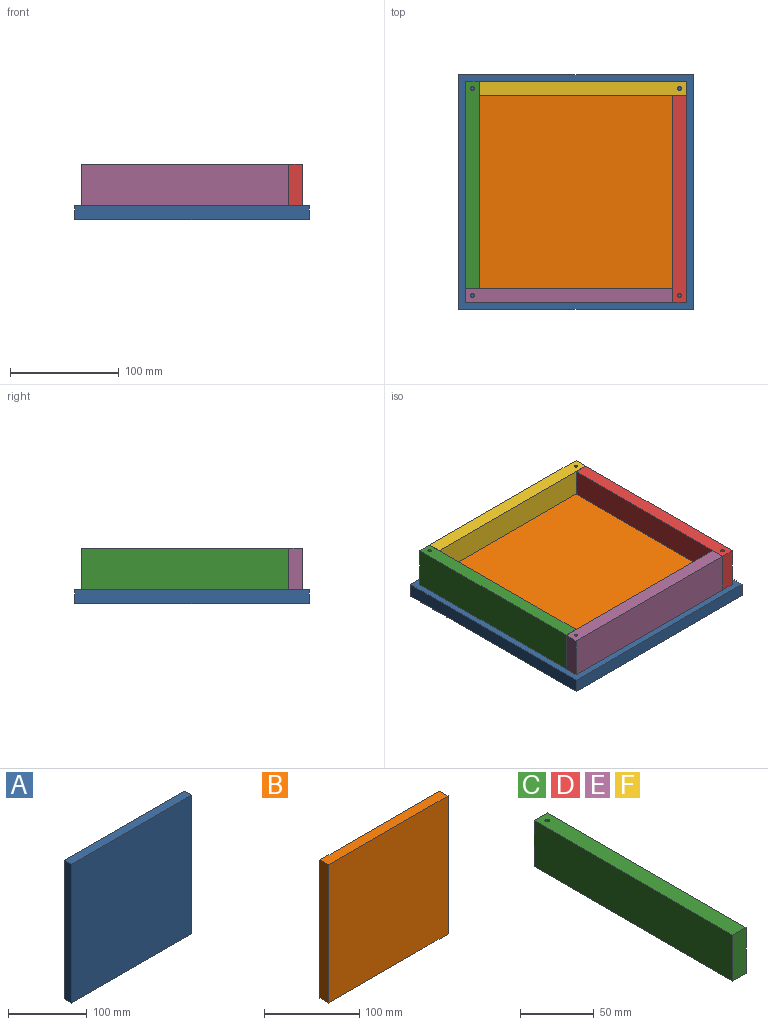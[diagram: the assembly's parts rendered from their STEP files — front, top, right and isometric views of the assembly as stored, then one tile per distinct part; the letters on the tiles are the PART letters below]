
ASSEMBLY  parts=6 mates=7
PART A: 6 faces, bbox 215.9x12.7x215.9 mm
  f0: plane 215.9x12.7mm, normal (0,0,1), area 2741.9mm2, adj f1,f3,f4,f5
  f1: plane 215.9x12.7mm, normal (-1,0,0), area 2741.9mm2, adj f0,f2,f4,f5
  f2: plane 215.9x12.7mm, normal (0,0,-1), area 2741.9mm2, adj f1,f3,f4,f5
  f3: plane 215.9x12.7mm, normal (1,0,0), area 2741.9mm2, adj f0,f2,f4,f5
  f4: plane 215.9x215.9mm, normal (0,-1,0), area 46612.8mm2, adj f0,f1,f2,f3
  f5: plane 215.9x215.9mm, normal (0,1,0), area 46612.8mm2, adj f0,f1,f2,f3
PART B: 6 faces, bbox 177.8x12.7x177.8 mm
  f0: plane 177.8x12.7mm, normal (0,0,1), area 2258.1mm2, adj f1,f3,f4,f5
  f1: plane 177.8x12.7mm, normal (-1,0,0), area 2258.1mm2, adj f0,f2,f4,f5
  f2: plane 177.8x12.7mm, normal (0,0,-1), area 2258.1mm2, adj f1,f3,f4,f5
  f3: plane 177.8x12.7mm, normal (1,0,0), area 2258.1mm2, adj f0,f2,f4,f5
  f4: plane 177.8x177.8mm, normal (0,-1,0), area 31612.8mm2, adj f0,f1,f2,f3
  f5: plane 177.8x177.8mm, normal (0,1,0), area 31612.8mm2, adj f0,f1,f2,f3
PART C: 7 faces, bbox 12.7x190.5x38.1 mm
  f0: plane 190.5x12.7mm, normal (0,0,1), area 2411.4mm2, adj f1,f3,f4,f5,f6
  f1: plane 38.1x12.7mm, normal (0,-1,0), area 483.9mm2, adj f0,f2,f4,f5
  f2: plane 190.5x12.7mm, normal (0,0,-1), area 2411.4mm2, adj f1,f3,f4,f5,f6
  f3: plane 38.1x12.7mm, normal (0,1,0), area 483.9mm2, adj f0,f2,f4,f5
  f4: plane 190.5x38.1mm, normal (1,0,0), area 7258mm2, adj f0,f1,f2,f3
  f5: plane 190.5x38.1mm, normal (-1,0,0), area 7258mm2, adj f0,f1,f2,f3
  f6: cylinder r=1.59mm len=38.1mm, axis (0,0,-1), area 380mm2, adj f0,f2
PART D: same geometry as C
PART E: same geometry as C
PART F: same geometry as C
PLACE A rot(axis=(-1,0,0),90deg) t=(-1078.6,329.43,-583.64)mm
PLACE B rot(axis=(-1,0,0),90deg) t=(-1118.01,29.42,-570.94)mm
PLACE C rot(axis=(0,-1,0),180deg) t=(270.89,109.39,-678.23)mm
PLACE D rot(axis=(1,0,0),180deg) t=(448.69,31.02,-678.23)mm
PLACE E rot(axis=(0,0,1),90deg) t=(320.61,-31.4,-425.55)mm
PLACE F rot(axis=(0,0,-1),90deg) t=(398.98,171.8,-425.55)mm
MATE planar A.f4 <-> D.f0  axis (0,0,1) through (359.79,70.25,-570.94)mm
MATE fastened E.f3 <-> C.f4  axis (-1,0,0) through (258.19,-18.7,-551.89)mm
MATE parallel B.f3 <-> D.f5  axis (1,0,0) through (448.69,70.25,-558.24)mm
MATE parallel F.f4 <-> B.f0  axis (0,-1,0) through (366.14,159.1,-551.89)mm
MATE fastened D.f3 <-> E.f5  axis (0,-1,0) through (448.69,-31.4,-551.89)mm
MATE fastened F.f3 <-> D.f4  axis (1,0,0) through (461.39,159.1,-551.89)mm
MATE fastened B.f5 <-> A.f4  axis (0,0,-1) through (359.79,70.25,-570.94)mm
